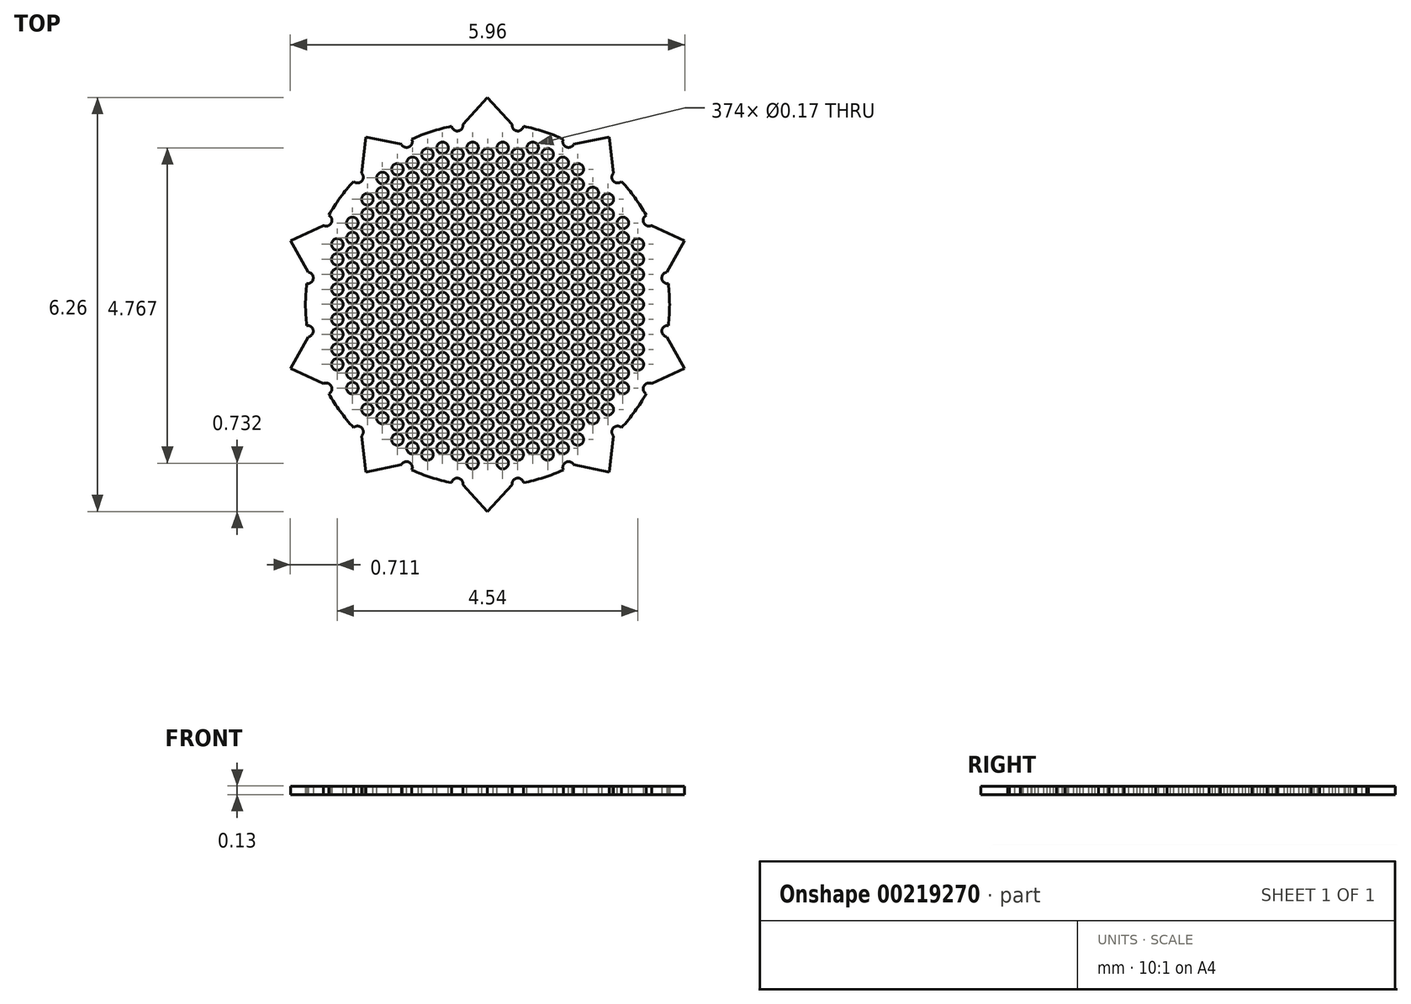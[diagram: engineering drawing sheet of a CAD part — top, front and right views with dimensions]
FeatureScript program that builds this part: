
annotation { "Feature Type Name" : "Feature", "Feature Type Description" : "" }
export const myFeature = defineFeature(function(context is Context, id is Id, definition is map)
    precondition{}
    {
        {
            var Q0;
            Q0=qCreatedBy(makeId("Top.planeOp"),FACE);
            var sketch = newSketch(context, id + "F0", { "sketchPlane" : qUnion([Q0])});
            skCircle(sketch, "E0", {"center": v(0, 0) * mm, "radius": 2.5 * mm});
            skArc(sketch, "E1", {"start": v(0.37, 2.72) * mm, "mid": v(0, 2.75) * mm, "end": v(-0.37, 2.72) * mm});
            skPoint(sketch, "E2", {"position": v(0, 2.75) * mm});
            skLineSegment(sketch, "E3", {"start": v(-3.94, 3.13) * mm, "end": v(3.7, 3.13) * mm, "construction": true});
            skLineSegment(sketch, "E4", {"start": v(0, 3.13) * mm, "end": v(-0.37, 2.72) * mm});
            skLineSegment(sketch, "E5", {"start": v(0, 3.13) * mm, "end": v(0.37, 2.72) * mm});
            skLineSegment(sketch, "E6.1.0", {"start": v(-1.84, 2.53) * mm, "end": v(-1.9, 1.99) * mm});
            skLineSegment(sketch, "E6.1.1", {"start": v(-1.84, 2.53) * mm, "end": v(-1.3, 2.42) * mm});
            skLineSegment(sketch, "E6.2.0", {"start": v(-2.98, 0.97) * mm, "end": v(-2.7, 0.49) * mm});
            skLineSegment(sketch, "E6.2.1", {"start": v(-2.98, 0.97) * mm, "end": v(-2.48, 1.2) * mm});
            skLineSegment(sketch, "E6.3.0", {"start": v(-2.98, -0.97) * mm, "end": v(-2.48, -1.2) * mm});
            skLineSegment(sketch, "E6.3.1", {"start": v(-2.98, -0.97) * mm, "end": v(-2.7, -0.49) * mm});
            skLineSegment(sketch, "E6.4.0", {"start": v(-1.84, -2.53) * mm, "end": v(-1.3, -2.42) * mm});
            skLineSegment(sketch, "E6.4.1", {"start": v(-1.84, -2.53) * mm, "end": v(-1.9, -1.99) * mm});
            skLineSegment(sketch, "E6.5.0", {"start": v(0, -3.13) * mm, "end": v(0.37, -2.72) * mm});
            skLineSegment(sketch, "E6.5.1", {"start": v(0, -3.13) * mm, "end": v(-0.37, -2.72) * mm});
            skLineSegment(sketch, "E6.6.0", {"start": v(1.84, -2.53) * mm, "end": v(1.9, -1.99) * mm});
            skLineSegment(sketch, "E6.6.1", {"start": v(1.84, -2.53) * mm, "end": v(1.3, -2.42) * mm});
            skLineSegment(sketch, "E6.7.0", {"start": v(2.98, -0.97) * mm, "end": v(2.7, -0.49) * mm});
            skLineSegment(sketch, "E6.7.1", {"start": v(2.98, -0.97) * mm, "end": v(2.48, -1.2) * mm});
            skLineSegment(sketch, "E6.8.0", {"start": v(2.98, 0.97) * mm, "end": v(2.48, 1.2) * mm});
            skLineSegment(sketch, "E6.8.1", {"start": v(2.98, 0.97) * mm, "end": v(2.7, 0.49) * mm});
            skLineSegment(sketch, "E6.9.0", {"start": v(1.84, 2.53) * mm, "end": v(1.3, 2.42) * mm});
            skLineSegment(sketch, "E6.9.1", {"start": v(1.84, 2.53) * mm, "end": v(1.9, 1.99) * mm});
            skCircle(sketch, "E7", {"center": v(0, 0) * mm, "radius": 2.62 * mm});
            skPoint(sketch, "E8", {"position": v(0.46, 2.71) * mm});
            skArc(sketch, "E9", {"start": v(0.37, 2.72) * mm, "mid": v(0.44, 2.63) * mm, "end": v(0.54, 2.7) * mm});
            skArc(sketch, "E10.1.0", {"start": v(-1.3, 2.42) * mm, "mid": v(-1.18, 2.38) * mm, "end": v(-1.14, 2.5) * mm});
            skArc(sketch, "E10.2.0", {"start": v(-2.48, 1.2) * mm, "mid": v(-2.36, 1.23) * mm, "end": v(-2.4, 1.35) * mm});
            skArc(sketch, "E10.3.0", {"start": v(-2.7, -0.49) * mm, "mid": v(-2.63, -0.4) * mm, "end": v(-2.73, -0.32) * mm});
            skArc(sketch, "E10.4.0", {"start": v(-1.9, -1.99) * mm, "mid": v(-1.9, -1.86) * mm, "end": v(-2.02, -1.86) * mm});
            skArc(sketch, "E10.5.0", {"start": v(-0.37, -2.72) * mm, "mid": v(-0.44, -2.63) * mm, "end": v(-0.54, -2.7) * mm});
            skArc(sketch, "E10.6.0", {"start": v(1.3, -2.42) * mm, "mid": v(1.18, -2.38) * mm, "end": v(1.14, -2.5) * mm});
            skArc(sketch, "E10.7.0", {"start": v(2.48, -1.2) * mm, "mid": v(2.36, -1.23) * mm, "end": v(2.4, -1.35) * mm});
            skArc(sketch, "E10.8.0", {"start": v(2.7, 0.49) * mm, "mid": v(2.63, 0.4) * mm, "end": v(2.73, 0.32) * mm});
            skArc(sketch, "E10.9.0", {"start": v(1.9, 1.99) * mm, "mid": v(1.9, 1.86) * mm, "end": v(2.02, 1.86) * mm});
            skArc(sketch, "E11", {"start": v(-0.54, 2.7) * mm, "mid": v(-0.44, 2.63) * mm, "end": v(-0.37, 2.72) * mm});
            skArc(sketch, "E12.trimOffspring", {"start": v(-0.54, 2.7) * mm, "mid": v(-0.85, 2.62) * mm, "end": v(-1.14, 2.5) * mm});
            skArc(sketch, "E13.1.0", {"start": v(-2.02, 1.86) * mm, "mid": v(-1.9, 1.86) * mm, "end": v(-1.9, 1.99) * mm});
            skArc(sketch, "E13.2.0", {"start": v(-2.73, 0.32) * mm, "mid": v(-2.63, 0.4) * mm, "end": v(-2.7, 0.49) * mm});
            skArc(sketch, "E13.3.0", {"start": v(-2.4, -1.35) * mm, "mid": v(-2.36, -1.23) * mm, "end": v(-2.48, -1.2) * mm});
            skArc(sketch, "E13.4.0", {"start": v(-1.14, -2.5) * mm, "mid": v(-1.18, -2.38) * mm, "end": v(-1.3, -2.42) * mm});
            skArc(sketch, "E13.5.0", {"start": v(0.54, -2.7) * mm, "mid": v(0.44, -2.63) * mm, "end": v(0.37, -2.72) * mm});
            skArc(sketch, "E13.6.0", {"start": v(2.02, -1.86) * mm, "mid": v(1.9, -1.86) * mm, "end": v(1.9, -1.99) * mm});
            skArc(sketch, "E13.7.0", {"start": v(2.73, -0.32) * mm, "mid": v(2.63, -0.4) * mm, "end": v(2.7, -0.49) * mm});
            skArc(sketch, "E13.8.0", {"start": v(2.4, 1.35) * mm, "mid": v(2.36, 1.23) * mm, "end": v(2.48, 1.2) * mm});
            skArc(sketch, "E13.9.0", {"start": v(1.14, 2.5) * mm, "mid": v(1.18, 2.38) * mm, "end": v(1.3, 2.42) * mm});
            skArc(sketch, "E14.trimOffspring", {"start": v(1.14, 2.5) * mm, "mid": v(0.85, 2.62) * mm, "end": v(0.54, 2.7) * mm});
            skArc(sketch, "E15.trimOffspring", {"start": v(1.9, 1.99) * mm, "mid": v(1.62, 2.22) * mm, "end": v(1.3, 2.42) * mm});
            skArc(sketch, "E16.trimOffspring", {"start": v(2.4, 1.35) * mm, "mid": v(2.22, 1.62) * mm, "end": v(2.02, 1.86) * mm});
            skArc(sketch, "E17.trimOffspring", {"start": v(2.7, 0.49) * mm, "mid": v(2.62, 0.85) * mm, "end": v(2.48, 1.2) * mm});
            skArc(sketch, "E18.trimOffspring", {"start": v(2.73, -0.32) * mm, "mid": v(2.75, 0) * mm, "end": v(2.73, 0.32) * mm});
            skArc(sketch, "E19.trimOffspring", {"start": v(2.48, -1.2) * mm, "mid": v(2.62, -0.85) * mm, "end": v(2.7, -0.49) * mm});
            skArc(sketch, "E20.trimOffspring", {"start": v(2.02, -1.86) * mm, "mid": v(2.22, -1.62) * mm, "end": v(2.4, -1.35) * mm});
            skArc(sketch, "E21.trimOffspring", {"start": v(1.3, -2.42) * mm, "mid": v(1.62, -2.22) * mm, "end": v(1.9, -1.99) * mm});
            skArc(sketch, "E22.trimOffspring", {"start": v(-2.4, -1.35) * mm, "mid": v(-2.22, -1.62) * mm, "end": v(-2.02, -1.86) * mm});
            skArc(sketch, "E23.trimOffspring", {"start": v(-1.9, -1.99) * mm, "mid": v(-1.62, -2.22) * mm, "end": v(-1.3, -2.42) * mm});
            skArc(sketch, "E24.trimOffspring", {"start": v(-1.14, -2.5) * mm, "mid": v(-0.85, -2.62) * mm, "end": v(-0.54, -2.7) * mm});
            skArc(sketch, "E25.trimOffspring", {"start": v(-0.37, -2.72) * mm, "mid": v(0, -2.75) * mm, "end": v(0.37, -2.72) * mm});
            skArc(sketch, "E26.trimOffspring", {"start": v(0.54, -2.7) * mm, "mid": v(0.85, -2.62) * mm, "end": v(1.14, -2.5) * mm});
            skArc(sketch, "E27.trimOffspring", {"start": v(-2.7, -0.49) * mm, "mid": v(-2.62, -0.85) * mm, "end": v(-2.48, -1.2) * mm});
            skArc(sketch, "E28.trimOffspring", {"start": v(-2.73, 0.32) * mm, "mid": v(-2.75, 0) * mm, "end": v(-2.73, -0.32) * mm});
            skArc(sketch, "E29.trimOffspring", {"start": v(-2.48, 1.2) * mm, "mid": v(-2.62, 0.85) * mm, "end": v(-2.7, 0.49) * mm});
            skArc(sketch, "E30.trimOffspring", {"start": v(-2.02, 1.86) * mm, "mid": v(-2.22, 1.62) * mm, "end": v(-2.4, 1.35) * mm});
            skArc(sketch, "E31.trimOffspring", {"start": v(-1.3, 2.42) * mm, "mid": v(-1.62, 2.22) * mm, "end": v(-1.9, 1.99) * mm});
            skSolve(sketch);
        }
        {
            var Q0;
            Q0 = qSketchRegion(id + "F0", true);
            var Q1;
            Q1=makeQuery(id+"F0.imprint","IMPRINT",FACE,{"disambiguationData":[TD([[makeQuery(id+"F0.imprint","IMPRINT",EDGE,{"derivedFrom":sQuery(id+"F0.wireOp",EDGE,"E0")}),1.0]])]});
            var Q2;
            Q2=makeQuery(id+"F0.imprint","IMPRINT",FACE,{"disambiguationData":[TD([[makeQuery(id+"F0.imprint","IMPRINT",EDGE,{"derivedFrom":sQuery(id+"F0.wireOp",EDGE,"E0")}),-1.0]])]});
            extrude(context, id + "F1", {"entities" : qUnion([Q0, Q1, Q2]), "depth" : 0.13 * mm});
        }
        {
            var Q0;
            Q0=makeQuery(id+"F1.opExtrude","CAP_FACE",FACE,{"disambiguationData":[OSD([sQuery(id+"F0.wireOp",EDGE,"E1"),sQuery(id+"F0.wireOp",EDGE,"E4"),sQuery(id+"F0.wireOp",EDGE,"E5"),sQuery(id+"F0.wireOp",EDGE,"E6.1.0"),sQuery(id+"F0.wireOp",EDGE,"E6.1.1"),sQuery(id+"F0.wireOp",EDGE,"E6.2.0"),sQuery(id+"F0.wireOp",EDGE,"E6.2.1"),sQuery(id+"F0.wireOp",EDGE,"E6.3.0"),sQuery(id+"F0.wireOp",EDGE,"E6.3.1"),sQuery(id+"F0.wireOp",EDGE,"E6.4.0"),sQuery(id+"F0.wireOp",EDGE,"E6.4.1"),sQuery(id+"F0.wireOp",EDGE,"E6.5.0"),sQuery(id+"F0.wireOp",EDGE,"E6.5.1"),sQuery(id+"F0.wireOp",EDGE,"E6.6.0"),sQuery(id+"F0.wireOp",EDGE,"E6.6.1"),sQuery(id+"F0.wireOp",EDGE,"E6.7.0"),sQuery(id+"F0.wireOp",EDGE,"E6.7.1"),sQuery(id+"F0.wireOp",EDGE,"E6.8.0"),sQuery(id+"F0.wireOp",EDGE,"E6.8.1"),sQuery(id+"F0.wireOp",EDGE,"E6.9.0"),sQuery(id+"F0.wireOp",EDGE,"E6.9.1")])],"isStart":false});
            cPlane(context, id + "F2", {"entities" : qUnion([Q0]), "cplaneType" : CPlaneType.OFFSET, "offset" : 0 * mm, "width" : 150 * mm, "height" : 150 * mm});
        }
        {
            var Q0;
            Q0=qCreatedBy(id+"F2.planeOp",FACE);
            var sketch = newSketch(context, id + "F3", { "sketchPlane" : qUnion([Q0])});
            skCircle(sketch, "E32.2.1.8", {"center": v(-2.04, 1.23) * mm, "radius": 0.09 * mm});
            skCircle(sketch, "E32.2.1.9", {"center": v(-2.04, 1) * mm, "radius": 0.09 * mm});
            skCircle(sketch, "E32.0.1.10", {"center": v(-2.27, 0.91) * mm, "radius": 0.09 * mm});
            skCircle(sketch, "E32.2.1.10", {"center": v(-2.04, 0.78) * mm, "radius": 0.09 * mm});
            skCircle(sketch, "E32.2.2.5", {"center": v(-1.59, 1.91) * mm, "radius": 0.09 * mm});
            skCircle(sketch, "E32.2.2.6", {"center": v(-1.59, 1.69) * mm, "radius": 0.09 * mm});
            skCircle(sketch, "E32.0.2.7", {"center": v(-1.82, 1.6) * mm, "radius": 0.09 * mm});
            skCircle(sketch, "E32.2.2.7", {"center": v(-1.59, 1.46) * mm, "radius": 0.09 * mm});
            skCircle(sketch, "E32.0.2.8", {"center": v(-1.82, 1.36) * mm, "radius": 0.09 * mm});
            skCircle(sketch, "E32.2.2.8", {"center": v(-1.59, 1.23) * mm, "radius": 0.09 * mm});
            skCircle(sketch, "E32.0.2.9", {"center": v(-1.82, 1.14) * mm, "radius": 0.09 * mm});
            skCircle(sketch, "E32.2.2.9", {"center": v(-1.59, 1) * mm, "radius": 0.09 * mm});
            skCircle(sketch, "E32.0.2.10", {"center": v(-1.82, 0.91) * mm, "radius": 0.09 * mm});
            skCircle(sketch, "E32.2.2.10", {"center": v(-1.59, 0.78) * mm, "radius": 0.09 * mm});
            skCircle(sketch, "E32.2.3.4", {"center": v(-1.13, 2.14) * mm, "radius": 0.09 * mm});
            skCircle(sketch, "E32.0.3.5", {"center": v(-1.36, 2.05) * mm, "radius": 0.09 * mm});
            skCircle(sketch, "E32.2.3.5", {"center": v(-1.13, 1.91) * mm, "radius": 0.09 * mm});
            skCircle(sketch, "E32.0.3.6", {"center": v(-1.36, 1.82) * mm, "radius": 0.09 * mm});
            skCircle(sketch, "E32.2.3.6", {"center": v(-1.13, 1.69) * mm, "radius": 0.09 * mm});
            skCircle(sketch, "E32.0.3.7", {"center": v(-1.36, 1.6) * mm, "radius": 0.09 * mm});
            skCircle(sketch, "E32.2.3.7", {"center": v(-1.13, 1.46) * mm, "radius": 0.09 * mm});
            skCircle(sketch, "E32.0.3.8", {"center": v(-1.36, 1.36) * mm, "radius": 0.09 * mm});
            skCircle(sketch, "E32.2.3.8", {"center": v(-1.13, 1.23) * mm, "radius": 0.09 * mm});
            skCircle(sketch, "E32.0.3.9", {"center": v(-1.36, 1.14) * mm, "radius": 0.09 * mm});
            skCircle(sketch, "E32.2.3.9", {"center": v(-1.13, 1) * mm, "radius": 0.09 * mm});
            skCircle(sketch, "E32.0.3.10", {"center": v(-1.36, 0.91) * mm, "radius": 0.09 * mm});
            skCircle(sketch, "E32.2.3.10", {"center": v(-1.13, 0.78) * mm, "radius": 0.09 * mm});
            skCircle(sketch, "E32.2.4.3", {"center": v(-0.68, 2.37) * mm, "radius": 0.09 * mm});
            skCircle(sketch, "E32.0.4.4", {"center": v(-0.9, 2.27) * mm, "radius": 0.09 * mm});
            skCircle(sketch, "E32.2.4.4", {"center": v(-0.68, 2.14) * mm, "radius": 0.09 * mm});
            skCircle(sketch, "E32.0.4.5", {"center": v(-0.9, 2.05) * mm, "radius": 0.09 * mm});
            skCircle(sketch, "E32.2.4.5", {"center": v(-0.68, 1.91) * mm, "radius": 0.09 * mm});
            skCircle(sketch, "E32.0.4.6", {"center": v(-0.9, 1.82) * mm, "radius": 0.09 * mm});
            skCircle(sketch, "E32.2.4.6", {"center": v(-0.68, 1.69) * mm, "radius": 0.09 * mm});
            skCircle(sketch, "E32.0.4.7", {"center": v(-0.9, 1.6) * mm, "radius": 0.09 * mm});
            skCircle(sketch, "E32.2.4.7", {"center": v(-0.68, 1.46) * mm, "radius": 0.09 * mm});
            skCircle(sketch, "E32.0.4.8", {"center": v(-0.9, 1.36) * mm, "radius": 0.09 * mm});
            skCircle(sketch, "E32.2.4.8", {"center": v(-0.68, 1.23) * mm, "radius": 0.09 * mm});
            skCircle(sketch, "E32.0.4.9", {"center": v(-0.9, 1.14) * mm, "radius": 0.09 * mm});
            skCircle(sketch, "E32.2.4.9", {"center": v(-0.68, 1) * mm, "radius": 0.09 * mm});
            skCircle(sketch, "E32.0.4.10", {"center": v(-0.9, 0.91) * mm, "radius": 0.09 * mm});
            skCircle(sketch, "E32.2.4.10", {"center": v(-0.68, 0.78) * mm, "radius": 0.09 * mm});
            skCircle(sketch, "E32.2.5.3", {"center": v(-0.23, 2.37) * mm, "radius": 0.09 * mm});
            skCircle(sketch, "E32.0.5.4", {"center": v(-0.45, 2.27) * mm, "radius": 0.09 * mm});
            skCircle(sketch, "E32.2.5.4", {"center": v(-0.23, 2.14) * mm, "radius": 0.09 * mm});
            skCircle(sketch, "E32.0.5.5", {"center": v(-0.45, 2.05) * mm, "radius": 0.09 * mm});
            skCircle(sketch, "E32.2.5.5", {"center": v(-0.23, 1.91) * mm, "radius": 0.09 * mm});
            skCircle(sketch, "E32.0.5.6", {"center": v(-0.45, 1.82) * mm, "radius": 0.09 * mm});
            skCircle(sketch, "E32.2.5.6", {"center": v(-0.23, 1.69) * mm, "radius": 0.09 * mm});
            skCircle(sketch, "E32.0.5.7", {"center": v(-0.45, 1.6) * mm, "radius": 0.09 * mm});
            skCircle(sketch, "E32.2.5.7", {"center": v(-0.23, 1.46) * mm, "radius": 0.09 * mm});
            skCircle(sketch, "E32.0.5.8", {"center": v(-0.45, 1.36) * mm, "radius": 0.09 * mm});
            skCircle(sketch, "E32.2.5.8", {"center": v(-0.23, 1.23) * mm, "radius": 0.09 * mm});
            skCircle(sketch, "E32.0.5.9", {"center": v(-0.45, 1.14) * mm, "radius": 0.09 * mm});
            skCircle(sketch, "E32.2.5.9", {"center": v(-0.23, 1) * mm, "radius": 0.09 * mm});
            skCircle(sketch, "E32.0.5.10", {"center": v(-0.45, 0.91) * mm, "radius": 0.09 * mm});
            skCircle(sketch, "E32.2.5.10", {"center": v(-0.23, 0.78) * mm, "radius": 0.09 * mm});
            skCircle(sketch, "E32.2.6.3", {"center": v(0.23, 2.37) * mm, "radius": 0.09 * mm});
            skCircle(sketch, "E32.0.6.4", {"center": v(0, 2.27) * mm, "radius": 0.09 * mm});
            skCircle(sketch, "E32.2.6.4", {"center": v(0.23, 2.14) * mm, "radius": 0.09 * mm});
            skCircle(sketch, "E32.0.6.5", {"center": v(0, 2.05) * mm, "radius": 0.09 * mm});
            skCircle(sketch, "E32.2.6.5", {"center": v(0.23, 1.91) * mm, "radius": 0.09 * mm});
            skCircle(sketch, "E32.0.6.6", {"center": v(0, 1.82) * mm, "radius": 0.09 * mm});
            skCircle(sketch, "E32.2.6.6", {"center": v(0.23, 1.69) * mm, "radius": 0.09 * mm});
            skCircle(sketch, "E32.0.6.7", {"center": v(0, 1.6) * mm, "radius": 0.09 * mm});
            skCircle(sketch, "E32.2.6.7", {"center": v(0.23, 1.46) * mm, "radius": 0.09 * mm});
            skCircle(sketch, "E32.0.6.8", {"center": v(0, 1.36) * mm, "radius": 0.09 * mm});
            skCircle(sketch, "E32.2.6.8", {"center": v(0.23, 1.23) * mm, "radius": 0.09 * mm});
            skCircle(sketch, "E32.0.6.9", {"center": v(0, 1.14) * mm, "radius": 0.09 * mm});
            skCircle(sketch, "E32.2.6.9", {"center": v(0.23, 1) * mm, "radius": 0.09 * mm});
            skCircle(sketch, "E32.0.6.10", {"center": v(0, 0.91) * mm, "radius": 0.09 * mm});
            skCircle(sketch, "E32.2.6.10", {"center": v(0.23, 0.78) * mm, "radius": 0.09 * mm});
            skCircle(sketch, "E32.2.7.3", {"center": v(0.68, 2.37) * mm, "radius": 0.09 * mm});
            skCircle(sketch, "E32.0.7.4", {"center": v(0.45, 2.27) * mm, "radius": 0.09 * mm});
            skCircle(sketch, "E32.2.7.4", {"center": v(0.68, 2.14) * mm, "radius": 0.09 * mm});
            skCircle(sketch, "E32.0.7.5", {"center": v(0.45, 2.05) * mm, "radius": 0.09 * mm});
            skCircle(sketch, "E32.2.7.5", {"center": v(0.68, 1.91) * mm, "radius": 0.09 * mm});
            skCircle(sketch, "E32.0.7.6", {"center": v(0.45, 1.82) * mm, "radius": 0.09 * mm});
            skCircle(sketch, "E32.2.7.6", {"center": v(0.68, 1.69) * mm, "radius": 0.09 * mm});
            skCircle(sketch, "E32.0.7.7", {"center": v(0.45, 1.6) * mm, "radius": 0.09 * mm});
            skCircle(sketch, "E32.2.7.7", {"center": v(0.68, 1.46) * mm, "radius": 0.09 * mm});
            skCircle(sketch, "E32.0.7.8", {"center": v(0.45, 1.36) * mm, "radius": 0.09 * mm});
            skCircle(sketch, "E32.2.7.8", {"center": v(0.68, 1.23) * mm, "radius": 0.09 * mm});
            skCircle(sketch, "E32.0.7.9", {"center": v(0.45, 1.14) * mm, "radius": 0.09 * mm});
            skCircle(sketch, "E32.2.7.9", {"center": v(0.68, 1) * mm, "radius": 0.09 * mm});
            skCircle(sketch, "E32.0.7.10", {"center": v(0.45, 0.91) * mm, "radius": 0.09 * mm});
            skCircle(sketch, "E32.2.7.10", {"center": v(0.68, 0.78) * mm, "radius": 0.09 * mm});
            skCircle(sketch, "E32.0.8.4", {"center": v(0.9, 2.27) * mm, "radius": 0.09 * mm});
            skCircle(sketch, "E32.2.8.4", {"center": v(1.14, 2.14) * mm, "radius": 0.09 * mm});
            skCircle(sketch, "E32.0.8.5", {"center": v(0.9, 2.05) * mm, "radius": 0.09 * mm});
            skCircle(sketch, "E32.2.8.5", {"center": v(1.14, 1.91) * mm, "radius": 0.09 * mm});
            skCircle(sketch, "E32.0.8.6", {"center": v(0.9, 1.82) * mm, "radius": 0.09 * mm});
            skCircle(sketch, "E32.2.8.6", {"center": v(1.14, 1.69) * mm, "radius": 0.09 * mm});
            skCircle(sketch, "E32.0.8.7", {"center": v(0.9, 1.6) * mm, "radius": 0.09 * mm});
            skCircle(sketch, "E32.2.8.7", {"center": v(1.14, 1.46) * mm, "radius": 0.09 * mm});
            skCircle(sketch, "E32.0.8.8", {"center": v(0.9, 1.36) * mm, "radius": 0.09 * mm});
            skCircle(sketch, "E32.2.8.8", {"center": v(1.14, 1.23) * mm, "radius": 0.09 * mm});
            skCircle(sketch, "E32.0.8.9", {"center": v(0.9, 1.14) * mm, "radius": 0.09 * mm});
            skCircle(sketch, "E32.2.8.9", {"center": v(1.14, 1) * mm, "radius": 0.09 * mm});
            skCircle(sketch, "E32.0.8.10", {"center": v(0.9, 0.91) * mm, "radius": 0.09 * mm});
            skCircle(sketch, "E32.2.8.10", {"center": v(1.14, 0.78) * mm, "radius": 0.09 * mm});
            skCircle(sketch, "E32.0.9.5", {"center": v(1.36, 2.05) * mm, "radius": 0.09 * mm});
            skCircle(sketch, "E32.0.9.6", {"center": v(1.36, 1.82) * mm, "radius": 0.09 * mm});
            skCircle(sketch, "E32.2.9.6", {"center": v(1.6, 1.69) * mm, "radius": 0.09 * mm});
            skCircle(sketch, "E32.0.9.7", {"center": v(1.36, 1.6) * mm, "radius": 0.09 * mm});
            skCircle(sketch, "E32.2.9.7", {"center": v(1.6, 1.46) * mm, "radius": 0.09 * mm});
            skCircle(sketch, "E32.0.9.8", {"center": v(1.36, 1.36) * mm, "radius": 0.09 * mm});
            skCircle(sketch, "E32.2.9.8", {"center": v(1.6, 1.23) * mm, "radius": 0.09 * mm});
            skCircle(sketch, "E32.0.9.9", {"center": v(1.36, 1.14) * mm, "radius": 0.09 * mm});
            skCircle(sketch, "E32.2.9.9", {"center": v(1.6, 1) * mm, "radius": 0.09 * mm});
            skCircle(sketch, "E32.0.9.10", {"center": v(1.36, 0.91) * mm, "radius": 0.09 * mm});
            skCircle(sketch, "E32.2.9.10", {"center": v(1.6, 0.78) * mm, "radius": 0.09 * mm});
            skCircle(sketch, "E32.0.10.7", {"center": v(1.82, 1.6) * mm, "radius": 0.09 * mm});
            skCircle(sketch, "E32.0.10.8", {"center": v(1.82, 1.36) * mm, "radius": 0.09 * mm});
            skCircle(sketch, "E32.2.10.8", {"center": v(2.04, 1.23) * mm, "radius": 0.09 * mm});
            skCircle(sketch, "E32.0.10.9", {"center": v(1.82, 1.14) * mm, "radius": 0.09 * mm});
            skCircle(sketch, "E32.2.10.9", {"center": v(2.04, 1) * mm, "radius": 0.09 * mm});
            skCircle(sketch, "E32.0.10.10", {"center": v(1.82, 0.91) * mm, "radius": 0.09 * mm});
            skCircle(sketch, "E32.2.10.10", {"center": v(2.04, 0.78) * mm, "radius": 0.09 * mm});
            skCircle(sketch, "E33.0.1.11", {"center": v(-2.27, 0.68) * mm, "radius": 0.09 * mm});
            skCircle(sketch, "E33.2.1.11", {"center": v(-2.04, 0.55) * mm, "radius": 0.09 * mm});
            skCircle(sketch, "E33.0.1.12", {"center": v(-2.27, 0.46) * mm, "radius": 0.09 * mm});
            skCircle(sketch, "E33.2.1.12", {"center": v(-2.04, 0.33) * mm, "radius": 0.09 * mm});
            skCircle(sketch, "E33.0.1.13", {"center": v(-2.27, 0.23) * mm, "radius": 0.09 * mm});
            skCircle(sketch, "E33.2.1.13", {"center": v(-2.04, 0.1) * mm, "radius": 0.09 * mm});
            skCircle(sketch, "E33.0.1.14", {"center": v(-2.27, 0) * mm, "radius": 0.09 * mm});
            skCircle(sketch, "E33.2.1.14", {"center": v(-2.04, -0.13) * mm, "radius": 0.09 * mm});
            skCircle(sketch, "E33.0.1.15", {"center": v(-2.27, -0.22) * mm, "radius": 0.09 * mm});
            skCircle(sketch, "E33.2.1.15", {"center": v(-2.04, -0.36) * mm, "radius": 0.09 * mm});
            skCircle(sketch, "E33.0.1.16", {"center": v(-2.27, -0.45) * mm, "radius": 0.09 * mm});
            skCircle(sketch, "E33.2.1.16", {"center": v(-2.04, -0.58) * mm, "radius": 0.09 * mm});
            skCircle(sketch, "E33.0.1.17", {"center": v(-2.27, -0.68) * mm, "radius": 0.09 * mm});
            skCircle(sketch, "E33.2.1.17", {"center": v(-2.04, -0.8) * mm, "radius": 0.09 * mm});
            skCircle(sketch, "E33.0.1.18", {"center": v(-2.27, -0.9) * mm, "radius": 0.09 * mm});
            skCircle(sketch, "E33.2.1.18", {"center": v(-2.04, -1.04) * mm, "radius": 0.09 * mm});
            skCircle(sketch, "E33.2.1.19", {"center": v(-2.04, -1.26) * mm, "radius": 0.09 * mm});
            skCircle(sketch, "E33.0.2.11", {"center": v(-1.82, 0.68) * mm, "radius": 0.09 * mm});
            skCircle(sketch, "E33.2.2.11", {"center": v(-1.59, 0.55) * mm, "radius": 0.09 * mm});
            skCircle(sketch, "E33.0.2.12", {"center": v(-1.82, 0.46) * mm, "radius": 0.09 * mm});
            skCircle(sketch, "E33.2.2.12", {"center": v(-1.59, 0.33) * mm, "radius": 0.09 * mm});
            skCircle(sketch, "E33.0.2.13", {"center": v(-1.82, 0.23) * mm, "radius": 0.09 * mm});
            skCircle(sketch, "E33.2.2.13", {"center": v(-1.59, 0.1) * mm, "radius": 0.09 * mm});
            skCircle(sketch, "E33.0.2.14", {"center": v(-1.82, 0) * mm, "radius": 0.09 * mm});
            skCircle(sketch, "E33.2.2.14", {"center": v(-1.59, -0.13) * mm, "radius": 0.09 * mm});
            skCircle(sketch, "E33.0.2.15", {"center": v(-1.82, -0.22) * mm, "radius": 0.09 * mm});
            skCircle(sketch, "E33.2.2.15", {"center": v(-1.59, -0.36) * mm, "radius": 0.09 * mm});
            skCircle(sketch, "E33.0.2.16", {"center": v(-1.82, -0.45) * mm, "radius": 0.09 * mm});
            skCircle(sketch, "E33.2.2.16", {"center": v(-1.59, -0.58) * mm, "radius": 0.09 * mm});
            skCircle(sketch, "E33.0.2.17", {"center": v(-1.82, -0.68) * mm, "radius": 0.09 * mm});
            skCircle(sketch, "E33.2.2.17", {"center": v(-1.59, -0.8) * mm, "radius": 0.09 * mm});
            skCircle(sketch, "E33.0.2.18", {"center": v(-1.82, -0.9) * mm, "radius": 0.09 * mm});
            skCircle(sketch, "E33.2.2.18", {"center": v(-1.59, -1.04) * mm, "radius": 0.09 * mm});
            skCircle(sketch, "E33.0.2.19", {"center": v(-1.82, -1.13) * mm, "radius": 0.09 * mm});
            skCircle(sketch, "E33.2.2.19", {"center": v(-1.59, -1.26) * mm, "radius": 0.09 * mm});
            skCircle(sketch, "E33.0.2.20", {"center": v(-1.82, -1.36) * mm, "radius": 0.09 * mm});
            skCircle(sketch, "E33.2.2.20", {"center": v(-1.59, -1.5) * mm, "radius": 0.09 * mm});
            skCircle(sketch, "E33.0.2.21", {"center": v(-1.82, -1.59) * mm, "radius": 0.09 * mm});
            skCircle(sketch, "E33.2.2.21", {"center": v(-1.59, -1.72) * mm, "radius": 0.09 * mm});
            skCircle(sketch, "E33.0.3.11", {"center": v(-1.36, 0.68) * mm, "radius": 0.09 * mm});
            skCircle(sketch, "E33.2.3.11", {"center": v(-1.13, 0.55) * mm, "radius": 0.09 * mm});
            skCircle(sketch, "E33.0.3.12", {"center": v(-1.36, 0.46) * mm, "radius": 0.09 * mm});
            skCircle(sketch, "E33.2.3.12", {"center": v(-1.13, 0.33) * mm, "radius": 0.09 * mm});
            skCircle(sketch, "E33.0.3.13", {"center": v(-1.36, 0.23) * mm, "radius": 0.09 * mm});
            skCircle(sketch, "E33.2.3.13", {"center": v(-1.13, 0.1) * mm, "radius": 0.09 * mm});
            skCircle(sketch, "E33.0.3.14", {"center": v(-1.36, 0) * mm, "radius": 0.09 * mm});
            skCircle(sketch, "E33.2.3.14", {"center": v(-1.13, -0.13) * mm, "radius": 0.09 * mm});
            skCircle(sketch, "E33.0.3.15", {"center": v(-1.36, -0.22) * mm, "radius": 0.09 * mm});
            skCircle(sketch, "E33.2.3.15", {"center": v(-1.13, -0.36) * mm, "radius": 0.09 * mm});
            skCircle(sketch, "E33.0.3.16", {"center": v(-1.36, -0.45) * mm, "radius": 0.09 * mm});
            skCircle(sketch, "E33.2.3.16", {"center": v(-1.13, -0.58) * mm, "radius": 0.09 * mm});
            skCircle(sketch, "E33.0.3.17", {"center": v(-1.36, -0.68) * mm, "radius": 0.09 * mm});
            skCircle(sketch, "E33.2.3.17", {"center": v(-1.13, -0.8) * mm, "radius": 0.09 * mm});
            skCircle(sketch, "E33.0.3.18", {"center": v(-1.36, -0.9) * mm, "radius": 0.09 * mm});
            skCircle(sketch, "E33.2.3.18", {"center": v(-1.13, -1.04) * mm, "radius": 0.09 * mm});
            skCircle(sketch, "E33.0.3.19", {"center": v(-1.36, -1.13) * mm, "radius": 0.09 * mm});
            skCircle(sketch, "E33.2.3.19", {"center": v(-1.13, -1.26) * mm, "radius": 0.09 * mm});
            skCircle(sketch, "E33.0.3.20", {"center": v(-1.36, -1.36) * mm, "radius": 0.09 * mm});
            skCircle(sketch, "E33.2.3.20", {"center": v(-1.13, -1.5) * mm, "radius": 0.09 * mm});
            skCircle(sketch, "E33.0.3.21", {"center": v(-1.36, -1.59) * mm, "radius": 0.09 * mm});
            skCircle(sketch, "E33.2.3.21", {"center": v(-1.13, -1.72) * mm, "radius": 0.09 * mm});
            skCircle(sketch, "E33.0.4.11", {"center": v(-0.9, 0.68) * mm, "radius": 0.09 * mm});
            skCircle(sketch, "E33.2.4.11", {"center": v(-0.68, 0.55) * mm, "radius": 0.09 * mm});
            skCircle(sketch, "E33.0.4.12", {"center": v(-0.9, 0.46) * mm, "radius": 0.09 * mm});
            skCircle(sketch, "E33.2.4.12", {"center": v(-0.68, 0.33) * mm, "radius": 0.09 * mm});
            skCircle(sketch, "E33.0.4.13", {"center": v(-0.9, 0.23) * mm, "radius": 0.09 * mm});
            skCircle(sketch, "E33.2.4.13", {"center": v(-0.68, 0.1) * mm, "radius": 0.09 * mm});
            skCircle(sketch, "E33.0.4.14", {"center": v(-0.9, 0) * mm, "radius": 0.09 * mm});
            skCircle(sketch, "E33.2.4.14", {"center": v(-0.68, -0.13) * mm, "radius": 0.09 * mm});
            skCircle(sketch, "E33.0.4.15", {"center": v(-0.9, -0.22) * mm, "radius": 0.09 * mm});
            skCircle(sketch, "E33.2.4.15", {"center": v(-0.68, -0.36) * mm, "radius": 0.09 * mm});
            skCircle(sketch, "E33.0.4.16", {"center": v(-0.9, -0.45) * mm, "radius": 0.09 * mm});
            skCircle(sketch, "E33.2.4.16", {"center": v(-0.68, -0.58) * mm, "radius": 0.09 * mm});
            skCircle(sketch, "E33.0.4.17", {"center": v(-0.9, -0.68) * mm, "radius": 0.09 * mm});
            skCircle(sketch, "E33.2.4.17", {"center": v(-0.68, -0.8) * mm, "radius": 0.09 * mm});
            skCircle(sketch, "E33.0.4.18", {"center": v(-0.9, -0.9) * mm, "radius": 0.09 * mm});
            skCircle(sketch, "E33.2.4.18", {"center": v(-0.68, -1.04) * mm, "radius": 0.09 * mm});
            skCircle(sketch, "E33.0.4.19", {"center": v(-0.9, -1.13) * mm, "radius": 0.09 * mm});
            skCircle(sketch, "E33.2.4.19", {"center": v(-0.68, -1.26) * mm, "radius": 0.09 * mm});
            skCircle(sketch, "E33.0.4.20", {"center": v(-0.9, -1.36) * mm, "radius": 0.09 * mm});
            skCircle(sketch, "E33.2.4.20", {"center": v(-0.68, -1.5) * mm, "radius": 0.09 * mm});
            skCircle(sketch, "E33.0.4.21", {"center": v(-0.9, -1.59) * mm, "radius": 0.09 * mm});
            skCircle(sketch, "E33.2.4.21", {"center": v(-0.68, -1.72) * mm, "radius": 0.09 * mm});
            skCircle(sketch, "E33.0.5.11", {"center": v(-0.45, 0.68) * mm, "radius": 0.09 * mm});
            skCircle(sketch, "E33.2.5.11", {"center": v(-0.23, 0.55) * mm, "radius": 0.09 * mm});
            skCircle(sketch, "E33.0.5.12", {"center": v(-0.45, 0.46) * mm, "radius": 0.09 * mm});
            skCircle(sketch, "E33.2.5.12", {"center": v(-0.23, 0.33) * mm, "radius": 0.09 * mm});
            skCircle(sketch, "E33.0.5.13", {"center": v(-0.45, 0.23) * mm, "radius": 0.09 * mm});
            skCircle(sketch, "E33.2.5.13", {"center": v(-0.23, 0.1) * mm, "radius": 0.09 * mm});
            skCircle(sketch, "E33.0.5.14", {"center": v(-0.45, 0) * mm, "radius": 0.09 * mm});
            skCircle(sketch, "E33.2.5.14", {"center": v(-0.23, -0.13) * mm, "radius": 0.09 * mm});
            skCircle(sketch, "E33.0.5.15", {"center": v(-0.45, -0.22) * mm, "radius": 0.09 * mm});
            skCircle(sketch, "E33.2.5.15", {"center": v(-0.23, -0.36) * mm, "radius": 0.09 * mm});
            skCircle(sketch, "E33.0.5.16", {"center": v(-0.45, -0.45) * mm, "radius": 0.09 * mm});
            skCircle(sketch, "E33.2.5.16", {"center": v(-0.23, -0.58) * mm, "radius": 0.09 * mm});
            skCircle(sketch, "E33.0.5.17", {"center": v(-0.45, -0.68) * mm, "radius": 0.09 * mm});
            skCircle(sketch, "E33.2.5.17", {"center": v(-0.23, -0.8) * mm, "radius": 0.09 * mm});
            skCircle(sketch, "E33.0.5.18", {"center": v(-0.45, -0.9) * mm, "radius": 0.09 * mm});
            skCircle(sketch, "E33.2.5.18", {"center": v(-0.23, -1.04) * mm, "radius": 0.09 * mm});
            skCircle(sketch, "E33.0.5.19", {"center": v(-0.45, -1.13) * mm, "radius": 0.09 * mm});
            skCircle(sketch, "E33.2.5.19", {"center": v(-0.23, -1.26) * mm, "radius": 0.09 * mm});
            skCircle(sketch, "E33.0.5.20", {"center": v(-0.45, -1.36) * mm, "radius": 0.09 * mm});
            skCircle(sketch, "E33.2.5.20", {"center": v(-0.23, -1.5) * mm, "radius": 0.09 * mm});
            skCircle(sketch, "E33.0.5.21", {"center": v(-0.45, -1.59) * mm, "radius": 0.09 * mm});
            skCircle(sketch, "E33.2.5.21", {"center": v(-0.23, -1.72) * mm, "radius": 0.09 * mm});
            skCircle(sketch, "E33.0.6.11", {"center": v(0, 0.68) * mm, "radius": 0.09 * mm});
            skCircle(sketch, "E33.2.6.11", {"center": v(0.23, 0.55) * mm, "radius": 0.09 * mm});
            skCircle(sketch, "E33.0.6.12", {"center": v(0, 0.46) * mm, "radius": 0.09 * mm});
            skCircle(sketch, "E33.2.6.12", {"center": v(0.23, 0.33) * mm, "radius": 0.09 * mm});
            skCircle(sketch, "E33.0.6.13", {"center": v(0, 0.23) * mm, "radius": 0.09 * mm});
            skCircle(sketch, "E33.2.6.13", {"center": v(0.23, 0.1) * mm, "radius": 0.09 * mm});
            skCircle(sketch, "E33.0.6.14", {"center": v(0, 0) * mm, "radius": 0.09 * mm});
            skCircle(sketch, "E33.2.6.14", {"center": v(0.23, -0.13) * mm, "radius": 0.09 * mm});
            skCircle(sketch, "E33.0.6.15", {"center": v(0, -0.22) * mm, "radius": 0.09 * mm});
            skCircle(sketch, "E33.2.6.15", {"center": v(0.23, -0.36) * mm, "radius": 0.09 * mm});
            skCircle(sketch, "E33.0.6.16", {"center": v(0, -0.45) * mm, "radius": 0.09 * mm});
            skCircle(sketch, "E33.2.6.16", {"center": v(0.23, -0.58) * mm, "radius": 0.09 * mm});
            skCircle(sketch, "E33.0.6.17", {"center": v(0, -0.68) * mm, "radius": 0.09 * mm});
            skCircle(sketch, "E33.2.6.17", {"center": v(0.23, -0.8) * mm, "radius": 0.09 * mm});
            skCircle(sketch, "E33.0.6.18", {"center": v(0, -0.9) * mm, "radius": 0.09 * mm});
            skCircle(sketch, "E33.2.6.18", {"center": v(0.23, -1.04) * mm, "radius": 0.09 * mm});
            skCircle(sketch, "E33.0.6.19", {"center": v(0, -1.13) * mm, "radius": 0.09 * mm});
            skCircle(sketch, "E33.2.6.19", {"center": v(0.23, -1.26) * mm, "radius": 0.09 * mm});
            skCircle(sketch, "E33.0.6.20", {"center": v(0, -1.36) * mm, "radius": 0.09 * mm});
            skCircle(sketch, "E33.2.6.20", {"center": v(0.23, -1.5) * mm, "radius": 0.09 * mm});
            skCircle(sketch, "E33.0.6.21", {"center": v(0, -1.59) * mm, "radius": 0.09 * mm});
            skCircle(sketch, "E33.2.6.21", {"center": v(0.23, -1.72) * mm, "radius": 0.09 * mm});
            skCircle(sketch, "E33.0.7.11", {"center": v(0.45, 0.68) * mm, "radius": 0.09 * mm});
            skCircle(sketch, "E33.2.7.11", {"center": v(0.68, 0.55) * mm, "radius": 0.09 * mm});
            skCircle(sketch, "E33.0.7.12", {"center": v(0.45, 0.46) * mm, "radius": 0.09 * mm});
            skCircle(sketch, "E33.2.7.12", {"center": v(0.68, 0.33) * mm, "radius": 0.09 * mm});
            skCircle(sketch, "E33.0.7.13", {"center": v(0.45, 0.23) * mm, "radius": 0.09 * mm});
            skCircle(sketch, "E33.2.7.13", {"center": v(0.68, 0.1) * mm, "radius": 0.09 * mm});
            skCircle(sketch, "E33.0.7.14", {"center": v(0.45, 0) * mm, "radius": 0.09 * mm});
            skCircle(sketch, "E33.2.7.14", {"center": v(0.68, -0.13) * mm, "radius": 0.09 * mm});
            skCircle(sketch, "E33.0.7.15", {"center": v(0.45, -0.22) * mm, "radius": 0.09 * mm});
            skCircle(sketch, "E33.2.7.15", {"center": v(0.68, -0.36) * mm, "radius": 0.09 * mm});
            skCircle(sketch, "E33.0.7.16", {"center": v(0.45, -0.45) * mm, "radius": 0.09 * mm});
            skCircle(sketch, "E33.2.7.16", {"center": v(0.68, -0.58) * mm, "radius": 0.09 * mm});
            skCircle(sketch, "E33.0.7.17", {"center": v(0.45, -0.68) * mm, "radius": 0.09 * mm});
            skCircle(sketch, "E33.2.7.17", {"center": v(0.68, -0.8) * mm, "radius": 0.09 * mm});
            skCircle(sketch, "E33.0.7.18", {"center": v(0.45, -0.9) * mm, "radius": 0.09 * mm});
            skCircle(sketch, "E33.2.7.18", {"center": v(0.68, -1.04) * mm, "radius": 0.09 * mm});
            skCircle(sketch, "E33.0.7.19", {"center": v(0.45, -1.13) * mm, "radius": 0.09 * mm});
            skCircle(sketch, "E33.2.7.19", {"center": v(0.68, -1.26) * mm, "radius": 0.09 * mm});
            skCircle(sketch, "E33.0.7.20", {"center": v(0.45, -1.36) * mm, "radius": 0.09 * mm});
            skCircle(sketch, "E33.2.7.20", {"center": v(0.68, -1.5) * mm, "radius": 0.09 * mm});
            skCircle(sketch, "E33.0.7.21", {"center": v(0.45, -1.59) * mm, "radius": 0.09 * mm});
            skCircle(sketch, "E33.2.7.21", {"center": v(0.68, -1.72) * mm, "radius": 0.09 * mm});
            skCircle(sketch, "E33.0.8.11", {"center": v(0.9, 0.68) * mm, "radius": 0.09 * mm});
            skCircle(sketch, "E33.2.8.11", {"center": v(1.14, 0.55) * mm, "radius": 0.09 * mm});
            skCircle(sketch, "E33.0.8.12", {"center": v(0.9, 0.46) * mm, "radius": 0.09 * mm});
            skCircle(sketch, "E33.2.8.12", {"center": v(1.14, 0.33) * mm, "radius": 0.09 * mm});
            skCircle(sketch, "E33.0.8.13", {"center": v(0.9, 0.23) * mm, "radius": 0.09 * mm});
            skCircle(sketch, "E33.2.8.13", {"center": v(1.14, 0.1) * mm, "radius": 0.09 * mm});
            skCircle(sketch, "E33.0.8.14", {"center": v(0.9, 0) * mm, "radius": 0.09 * mm});
            skCircle(sketch, "E33.2.8.14", {"center": v(1.14, -0.13) * mm, "radius": 0.09 * mm});
            skCircle(sketch, "E33.0.8.15", {"center": v(0.9, -0.22) * mm, "radius": 0.09 * mm});
            skCircle(sketch, "E33.2.8.15", {"center": v(1.14, -0.36) * mm, "radius": 0.09 * mm});
            skCircle(sketch, "E33.0.8.16", {"center": v(0.9, -0.45) * mm, "radius": 0.09 * mm});
            skCircle(sketch, "E33.2.8.16", {"center": v(1.14, -0.58) * mm, "radius": 0.09 * mm});
            skCircle(sketch, "E33.0.8.17", {"center": v(0.9, -0.68) * mm, "radius": 0.09 * mm});
            skCircle(sketch, "E33.2.8.17", {"center": v(1.14, -0.8) * mm, "radius": 0.09 * mm});
            skCircle(sketch, "E33.0.8.18", {"center": v(0.9, -0.9) * mm, "radius": 0.09 * mm});
            skCircle(sketch, "E33.2.8.18", {"center": v(1.14, -1.04) * mm, "radius": 0.09 * mm});
            skCircle(sketch, "E33.0.8.19", {"center": v(0.9, -1.13) * mm, "radius": 0.09 * mm});
            skCircle(sketch, "E33.2.8.19", {"center": v(1.14, -1.26) * mm, "radius": 0.09 * mm});
            skCircle(sketch, "E33.0.8.20", {"center": v(0.9, -1.36) * mm, "radius": 0.09 * mm});
            skCircle(sketch, "E33.2.8.20", {"center": v(1.14, -1.5) * mm, "radius": 0.09 * mm});
            skCircle(sketch, "E33.0.8.21", {"center": v(0.9, -1.59) * mm, "radius": 0.09 * mm});
            skCircle(sketch, "E33.2.8.21", {"center": v(1.14, -1.72) * mm, "radius": 0.09 * mm});
            skCircle(sketch, "E33.0.9.11", {"center": v(1.36, 0.68) * mm, "radius": 0.09 * mm});
            skCircle(sketch, "E33.2.9.11", {"center": v(1.6, 0.55) * mm, "radius": 0.09 * mm});
            skCircle(sketch, "E33.0.9.12", {"center": v(1.36, 0.46) * mm, "radius": 0.09 * mm});
            skCircle(sketch, "E33.2.9.12", {"center": v(1.6, 0.33) * mm, "radius": 0.09 * mm});
            skCircle(sketch, "E33.0.9.13", {"center": v(1.36, 0.23) * mm, "radius": 0.09 * mm});
            skCircle(sketch, "E33.2.9.13", {"center": v(1.6, 0.1) * mm, "radius": 0.09 * mm});
            skCircle(sketch, "E33.0.9.14", {"center": v(1.36, 0) * mm, "radius": 0.09 * mm});
            skCircle(sketch, "E33.2.9.14", {"center": v(1.6, -0.13) * mm, "radius": 0.09 * mm});
            skCircle(sketch, "E33.0.9.15", {"center": v(1.36, -0.22) * mm, "radius": 0.09 * mm});
            skCircle(sketch, "E33.2.9.15", {"center": v(1.6, -0.36) * mm, "radius": 0.09 * mm});
            skCircle(sketch, "E33.0.9.16", {"center": v(1.36, -0.45) * mm, "radius": 0.09 * mm});
            skCircle(sketch, "E33.2.9.16", {"center": v(1.6, -0.58) * mm, "radius": 0.09 * mm});
            skCircle(sketch, "E33.0.9.17", {"center": v(1.36, -0.68) * mm, "radius": 0.09 * mm});
            skCircle(sketch, "E33.2.9.17", {"center": v(1.6, -0.8) * mm, "radius": 0.09 * mm});
            skCircle(sketch, "E33.0.9.18", {"center": v(1.36, -0.9) * mm, "radius": 0.09 * mm});
            skCircle(sketch, "E33.2.9.18", {"center": v(1.6, -1.04) * mm, "radius": 0.09 * mm});
            skCircle(sketch, "E33.0.9.19", {"center": v(1.36, -1.13) * mm, "radius": 0.09 * mm});
            skCircle(sketch, "E33.2.9.19", {"center": v(1.6, -1.26) * mm, "radius": 0.09 * mm});
            skCircle(sketch, "E33.0.9.20", {"center": v(1.36, -1.36) * mm, "radius": 0.09 * mm});
            skCircle(sketch, "E33.2.9.20", {"center": v(1.6, -1.5) * mm, "radius": 0.09 * mm});
            skCircle(sketch, "E33.0.9.21", {"center": v(1.36, -1.59) * mm, "radius": 0.09 * mm});
            skCircle(sketch, "E33.2.9.21", {"center": v(1.6, -1.72) * mm, "radius": 0.09 * mm});
            skCircle(sketch, "E33.0.10.11", {"center": v(1.82, 0.68) * mm, "radius": 0.09 * mm});
            skCircle(sketch, "E33.2.10.11", {"center": v(2.04, 0.55) * mm, "radius": 0.09 * mm});
            skCircle(sketch, "E33.0.10.12", {"center": v(1.82, 0.46) * mm, "radius": 0.09 * mm});
            skCircle(sketch, "E33.2.10.12", {"center": v(2.04, 0.33) * mm, "radius": 0.09 * mm});
            skCircle(sketch, "E33.0.10.13", {"center": v(1.82, 0.23) * mm, "radius": 0.09 * mm});
            skCircle(sketch, "E33.2.10.13", {"center": v(2.04, 0.1) * mm, "radius": 0.09 * mm});
            skCircle(sketch, "E33.0.10.14", {"center": v(1.82, 0) * mm, "radius": 0.09 * mm});
            skCircle(sketch, "E33.2.10.14", {"center": v(2.04, -0.13) * mm, "radius": 0.09 * mm});
            skCircle(sketch, "E33.0.10.15", {"center": v(1.82, -0.22) * mm, "radius": 0.09 * mm});
            skCircle(sketch, "E33.2.10.15", {"center": v(2.04, -0.36) * mm, "radius": 0.09 * mm});
            skCircle(sketch, "E33.0.10.16", {"center": v(1.82, -0.45) * mm, "radius": 0.09 * mm});
            skCircle(sketch, "E33.2.10.16", {"center": v(2.04, -0.58) * mm, "radius": 0.09 * mm});
            skCircle(sketch, "E33.0.10.17", {"center": v(1.82, -0.68) * mm, "radius": 0.09 * mm});
            skCircle(sketch, "E33.2.10.17", {"center": v(2.04, -0.8) * mm, "radius": 0.09 * mm});
            skCircle(sketch, "E33.0.10.18", {"center": v(1.82, -0.9) * mm, "radius": 0.09 * mm});
            skCircle(sketch, "E33.2.10.18", {"center": v(2.04, -1.04) * mm, "radius": 0.09 * mm});
            skCircle(sketch, "E33.0.10.19", {"center": v(1.82, -1.13) * mm, "radius": 0.09 * mm});
            skCircle(sketch, "E33.2.10.19", {"center": v(2.04, -1.26) * mm, "radius": 0.09 * mm});
            skCircle(sketch, "E33.0.10.20", {"center": v(1.82, -1.36) * mm, "radius": 0.09 * mm});
            skCircle(sketch, "E33.0.10.21", {"center": v(1.82, -1.59) * mm, "radius": 0.09 * mm});
            skCircle(sketch, "E34.0.11.10", {"center": v(2.27, 0.91) * mm, "radius": 0.09 * mm});
            skCircle(sketch, "E34.0.11.11", {"center": v(2.27, 0.68) * mm, "radius": 0.09 * mm});
            skCircle(sketch, "E34.0.11.12", {"center": v(2.27, 0.46) * mm, "radius": 0.09 * mm});
            skCircle(sketch, "E34.0.11.13", {"center": v(2.27, 0.23) * mm, "radius": 0.09 * mm});
            skCircle(sketch, "E34.0.11.14", {"center": v(2.27, 0) * mm, "radius": 0.09 * mm});
            skCircle(sketch, "E34.0.11.15", {"center": v(2.27, -0.22) * mm, "radius": 0.09 * mm});
            skCircle(sketch, "E34.0.11.16", {"center": v(2.27, -0.45) * mm, "radius": 0.09 * mm});
            skCircle(sketch, "E34.0.11.17", {"center": v(2.27, -0.68) * mm, "radius": 0.09 * mm});
            skCircle(sketch, "E34.0.11.18", {"center": v(2.27, -0.9) * mm, "radius": 0.09 * mm});
            skCircle(sketch, "E35.0.3.22", {"center": v(-1.36, -1.81) * mm, "radius": 0.09 * mm});
            skCircle(sketch, "E35.2.3.22", {"center": v(-1.13, -1.94) * mm, "radius": 0.09 * mm});
            skCircle(sketch, "E35.0.3.23", {"center": v(-1.36, -2.04) * mm, "radius": 0.09 * mm});
            skCircle(sketch, "E35.2.3.23", {"center": v(-1.13, -2.17) * mm, "radius": 0.09 * mm});
            skCircle(sketch, "E35.0.4.22", {"center": v(-0.9, -1.81) * mm, "radius": 0.09 * mm});
            skCircle(sketch, "E35.2.4.22", {"center": v(-0.68, -1.94) * mm, "radius": 0.09 * mm});
            skCircle(sketch, "E35.0.4.23", {"center": v(-0.9, -2.04) * mm, "radius": 0.09 * mm});
            skCircle(sketch, "E35.2.4.23", {"center": v(-0.68, -2.17) * mm, "radius": 0.09 * mm});
            skCircle(sketch, "E35.0.4.24", {"center": v(-0.9, -2.27) * mm, "radius": 0.09 * mm});
            skCircle(sketch, "E35.0.5.22", {"center": v(-0.45, -1.81) * mm, "radius": 0.09 * mm});
            skCircle(sketch, "E35.2.5.22", {"center": v(-0.23, -1.94) * mm, "radius": 0.09 * mm});
            skCircle(sketch, "E35.0.5.23", {"center": v(-0.45, -2.04) * mm, "radius": 0.09 * mm});
            skCircle(sketch, "E35.2.5.23", {"center": v(-0.23, -2.17) * mm, "radius": 0.09 * mm});
            skCircle(sketch, "E35.0.5.24", {"center": v(-0.45, -2.27) * mm, "radius": 0.09 * mm});
            skCircle(sketch, "E35.2.5.24", {"center": v(-0.23, -2.4) * mm, "radius": 0.09 * mm});
            skCircle(sketch, "E35.0.6.22", {"center": v(0, -1.81) * mm, "radius": 0.09 * mm});
            skCircle(sketch, "E35.2.6.22", {"center": v(0.23, -1.94) * mm, "radius": 0.09 * mm});
            skCircle(sketch, "E35.0.6.23", {"center": v(0, -2.04) * mm, "radius": 0.09 * mm});
            skCircle(sketch, "E35.2.6.23", {"center": v(0.23, -2.17) * mm, "radius": 0.09 * mm});
            skCircle(sketch, "E35.0.6.24", {"center": v(0, -2.27) * mm, "radius": 0.09 * mm});
            skCircle(sketch, "E35.2.6.24", {"center": v(0.23, -2.4) * mm, "radius": 0.09 * mm});
            skCircle(sketch, "E35.0.7.22", {"center": v(0.45, -1.81) * mm, "radius": 0.09 * mm});
            skCircle(sketch, "E35.2.7.22", {"center": v(0.68, -1.94) * mm, "radius": 0.09 * mm});
            skCircle(sketch, "E35.0.7.23", {"center": v(0.45, -2.04) * mm, "radius": 0.09 * mm});
            skCircle(sketch, "E35.2.7.23", {"center": v(0.68, -2.17) * mm, "radius": 0.09 * mm});
            skCircle(sketch, "E35.0.7.24", {"center": v(0.45, -2.27) * mm, "radius": 0.09 * mm});
            skCircle(sketch, "E35.0.8.22", {"center": v(0.9, -1.81) * mm, "radius": 0.09 * mm});
            skCircle(sketch, "E35.2.8.22", {"center": v(1.14, -1.94) * mm, "radius": 0.09 * mm});
            skCircle(sketch, "E35.0.8.23", {"center": v(0.9, -2.04) * mm, "radius": 0.09 * mm});
            skCircle(sketch, "E35.2.8.23", {"center": v(1.14, -2.17) * mm, "radius": 0.09 * mm});
            skCircle(sketch, "E35.0.8.24", {"center": v(0.9, -2.27) * mm, "radius": 0.09 * mm});
            skCircle(sketch, "E35.0.9.22", {"center": v(1.36, -1.81) * mm, "radius": 0.09 * mm});
            skCircle(sketch, "E35.0.9.23", {"center": v(1.36, -2.04) * mm, "radius": 0.09 * mm});
            skCircle(sketch, "E36.0", {"center": v(0, 0) * mm, "radius": 2.5 * mm, "construction": true});
            skSolve(sketch);
        }
        {
            var Q0;
            Q0 = qSketchRegion(id + "F3", true);
            extrude(context, id + "F4", {"entities" : qUnion([Q0]), "operationType" : NewBodyOperationType.REMOVE, "endBound" : BoundingType.THROUGH_ALL, "oppositeDirection" : true, "depth" : 25 * mm});
        }
    });
